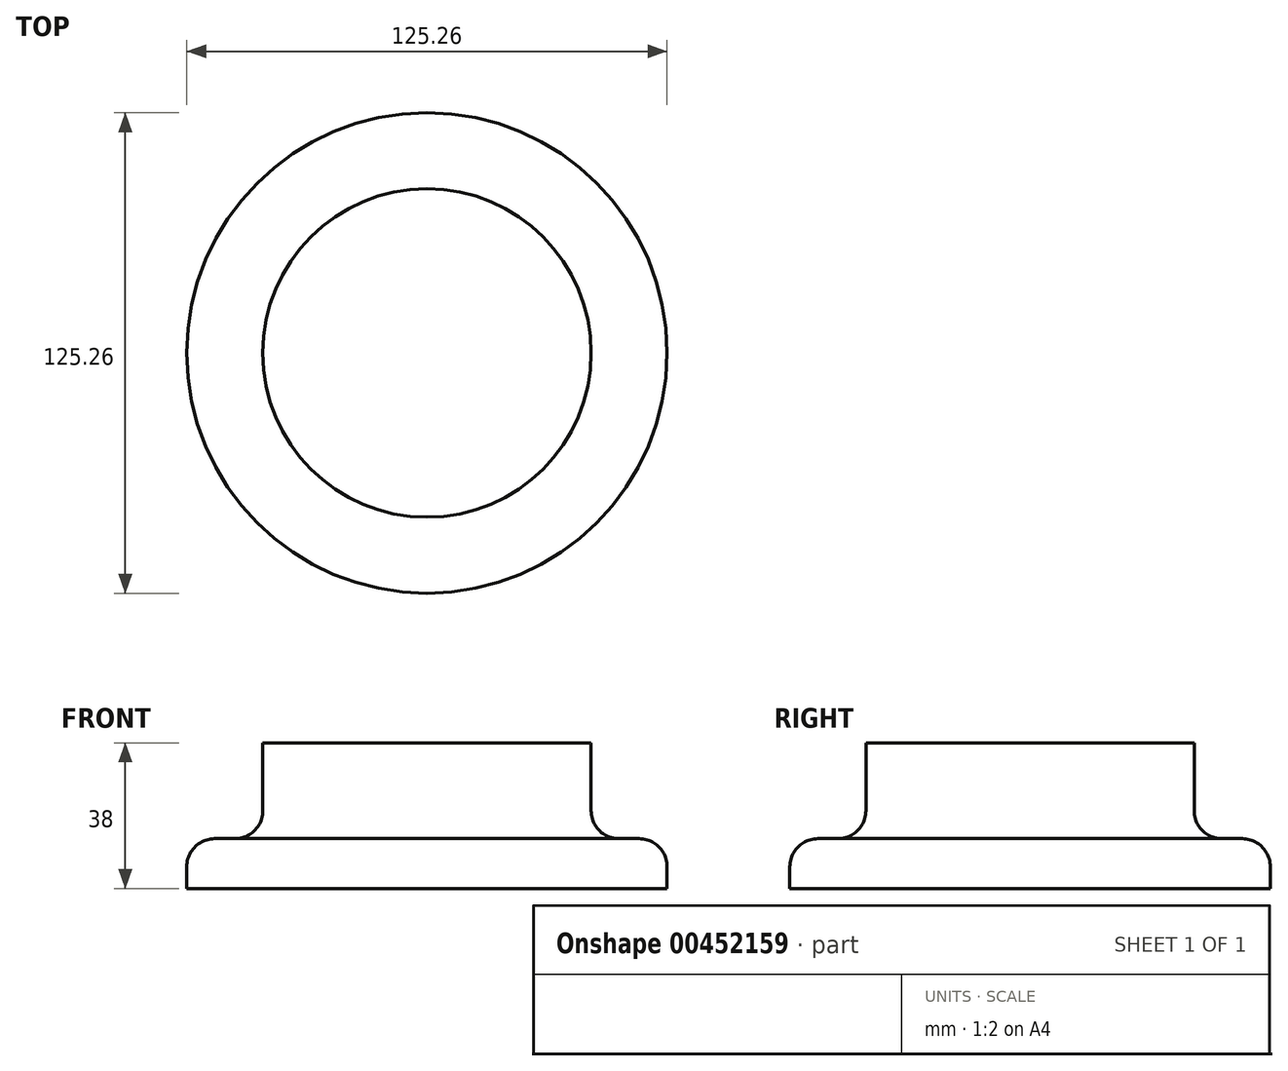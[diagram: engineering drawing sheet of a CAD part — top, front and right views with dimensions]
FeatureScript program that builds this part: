
annotation { "Feature Type Name" : "Feature", "Feature Type Description" : "" }
export const myFeature = defineFeature(function(context is Context, id is Id, definition is map)
    precondition{}
    {
        {
            var Q0;
            Q0=qCreatedBy(makeId("Top.planeOp"),FACE);
            var sketch = newSketch(context, id + "F0", { "sketchPlane" : qUnion([Q0])});
            skCircle(sketch, "E0", {"center": v(0, 0) * mm, "radius": 42.81 * mm});
            skSolve(sketch);
        }
        {
            var Q0;
            Q0 = qSketchRegion(id + "F0", true);
            extrude(context, id + "F1", {"entities" : qUnion([Q0]), "depth" : 25 * mm});
        }
        {
            var Q0;
            Q0=qCreatedBy(makeId("Top.planeOp"),FACE);
            var sketch = newSketch(context, id + "F2", { "sketchPlane" : qUnion([Q0])});
            skCircle(sketch, "E1", {"center": v(0, 0) * mm, "radius": 62.63 * mm});
            skSolve(sketch);
        }
        {
            var Q0;
            Q0 = qSketchRegion(id + "F2", true);
            extrude(context, id + "F3", {"entities" : qUnion([Q0]), "operationType" : NewBodyOperationType.ADD, "oppositeDirection" : true, "depth" : 13 * mm});
        }
        {
            var Q0;
            Q0=makeQuery(id+"F3.opExtrude","CAP_FACE",FACE,{"disambiguationData":[OSD([sQuery(id+"F2.wireOp",EDGE,"E1")])],"isStart":true});
            fillet(context, id + "F4", {"entities" : qUnion([Q0]), "radius" : 7.24 * mm, "tangentPropagation" : true, "allowEdgeOverflow" : false});
        }
    });
